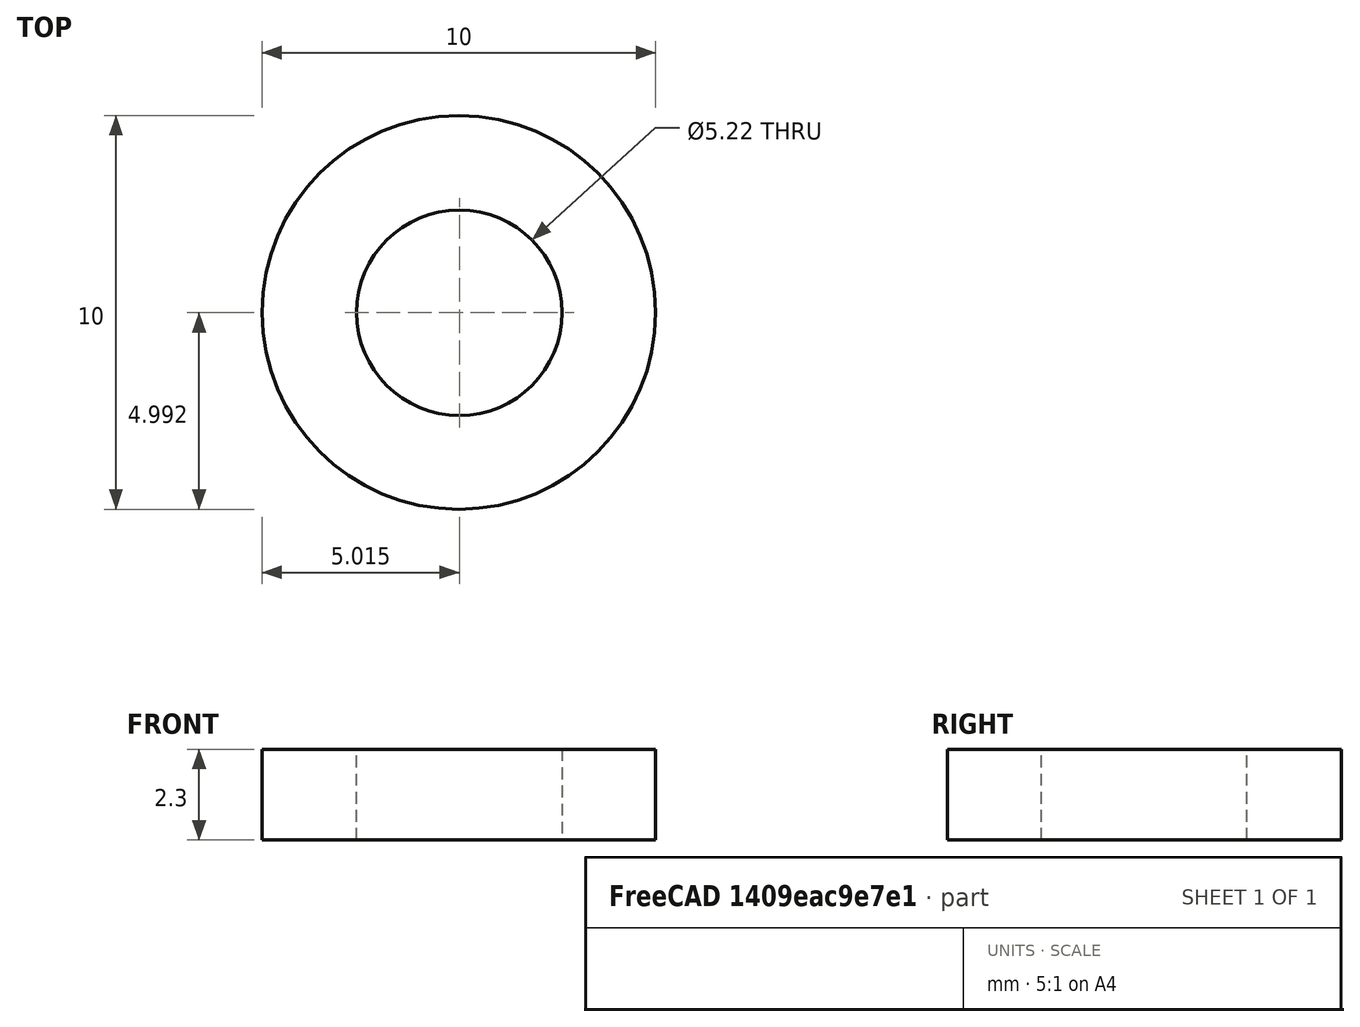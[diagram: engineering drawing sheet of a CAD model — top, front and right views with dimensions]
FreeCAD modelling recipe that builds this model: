
FCSTD DOCUMENT  (FreeCAD 0.18.4R)
Label: rondelle_visM5
License: All rights reserved
LicenseURL: http://en.wikipedia.org/wiki/All_rights_reserved
objects: Sketcher::SketchObject×2, PartDesign::Pad×1, PartDesign::Pocket×1, PartDesign::Body×1
note: 7 computed .brp shape members not serialized (recipe doc carries the construction recipe); baked Part::Feature solids carry a one-line shape summary decoded from their .brp

FEATURE [Sketcher::SketchObject] Sketch001
  MapMode = 5
  Support = -> [XY_Plane]
  sketch-geometry (1):
    g0: Circle CenterX=0 CenterY=0 CenterZ=0 NormalX=0 NormalY=0 NormalZ=1 AngleXU=0 Radius=5
  constraints (1):
    c: Radius(g0) = 5
FEATURE [PartDesign::Pad] Pad
  Length = 2.3
  Length2 = 100
  Profile = -> Sketch001
  Type = 0
FEATURE [Sketcher::SketchObject] Sketch
  MapMode = 5
  Placement = pos=(0,0,2.3) rot=(0,0,1;0rad)
  Support = -> [Pad]
  sketch-geometry (1):
    g0: Circle CenterX=0.015112 CenterY=-0.00765 CenterZ=0 NormalX=0 NormalY=0 NormalZ=1 AngleXU=0 Radius=2.61
  constraints (1):
    c: Radius(g0) = 2.61
FEATURE [PartDesign::Pocket] Pocket
  BaseFeature = -> Pad
  Length = 5
  Length2 = 100
  Profile = -> Sketch
  Type = 0
FEATURE [PartDesign::Body] Body
  Group = -> [Sketch001,Pad,Pocket]
  Origin = -> Origin
  Tip = -> Pocket
